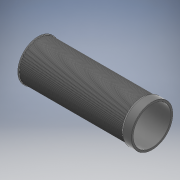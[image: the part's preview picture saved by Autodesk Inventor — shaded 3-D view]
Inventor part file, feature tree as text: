
AUTODESK INVENTOR PART (.ipt)
format: ipt  version: 2022 (Build 260153000, 153)  size: 176,640 bytes
history: native  units: mm
features: extrude x6, sketch x5, chamfer x2, fillet x2, plane x1
ambient origin geometry x8: Origin, YZ Plane, XZ Plane, XY Plane, X Axis, Y Axis, Z Axis, Center Point
bodies: Body1 (feature_tree)
feature tree (16):
  extrude  "Extrusion2"  Depth=4.0mm TaperAngle=0.0deg
  extrude  "Extrusion3"  Depth=40.0mm TaperAngle=0.0deg
  plane  "Work Plane1"
  extrude  "Extrusion4"  Depth=20.0mm TaperAngle=0.0deg
  chamfer  "Chamfer1"  Distance=40.0mm
  sketch  "Sketch7"  dims[d16=0.8mm d17=8.0mm d18=2.0mm d19=60.0deg]
  extrude  "Extrusion5"  Depth=0.8mm TaperAngle=60.0deg
  extrude  "Extrusion6"  TaperAngle=0.0deg  [1 undecoded]
  fillet  "Fillet1"  Radius=0.5mm
  chamfer  "Chamfer2"  Distance=0.872665mm
  fillet  "Fillet2"  [1 undecoded]
  extrude  "Extrusion7"  [1 undecoded]
  sketch  "Sketch8"  dims[d20=1.0mm d21=0.0mm d22=0.0mm d0=0.5mm d1=0.872665mm d23=0.0mm]
  sketch  "Sketch3"  dims[d2=4.0mm d3=0.0mm d4=400.0mm d5=0.0mm]
  sketch  "Sketch4"  dims[d6=400.0mm d7=40.0mm d8=0.0mm]
  sketch  "Sketch5"  dims[d9=4.0mm d10=2.0mm d11=60.0deg d12=20.0mm d13=0.0mm d14=40.0mm d15=0.0mm]
note: 3 required parameter values undecoded (feature->parameter linkage not recoverable at this tier; creation-order binding heuristic only, values carry confidence <= 0.55)
